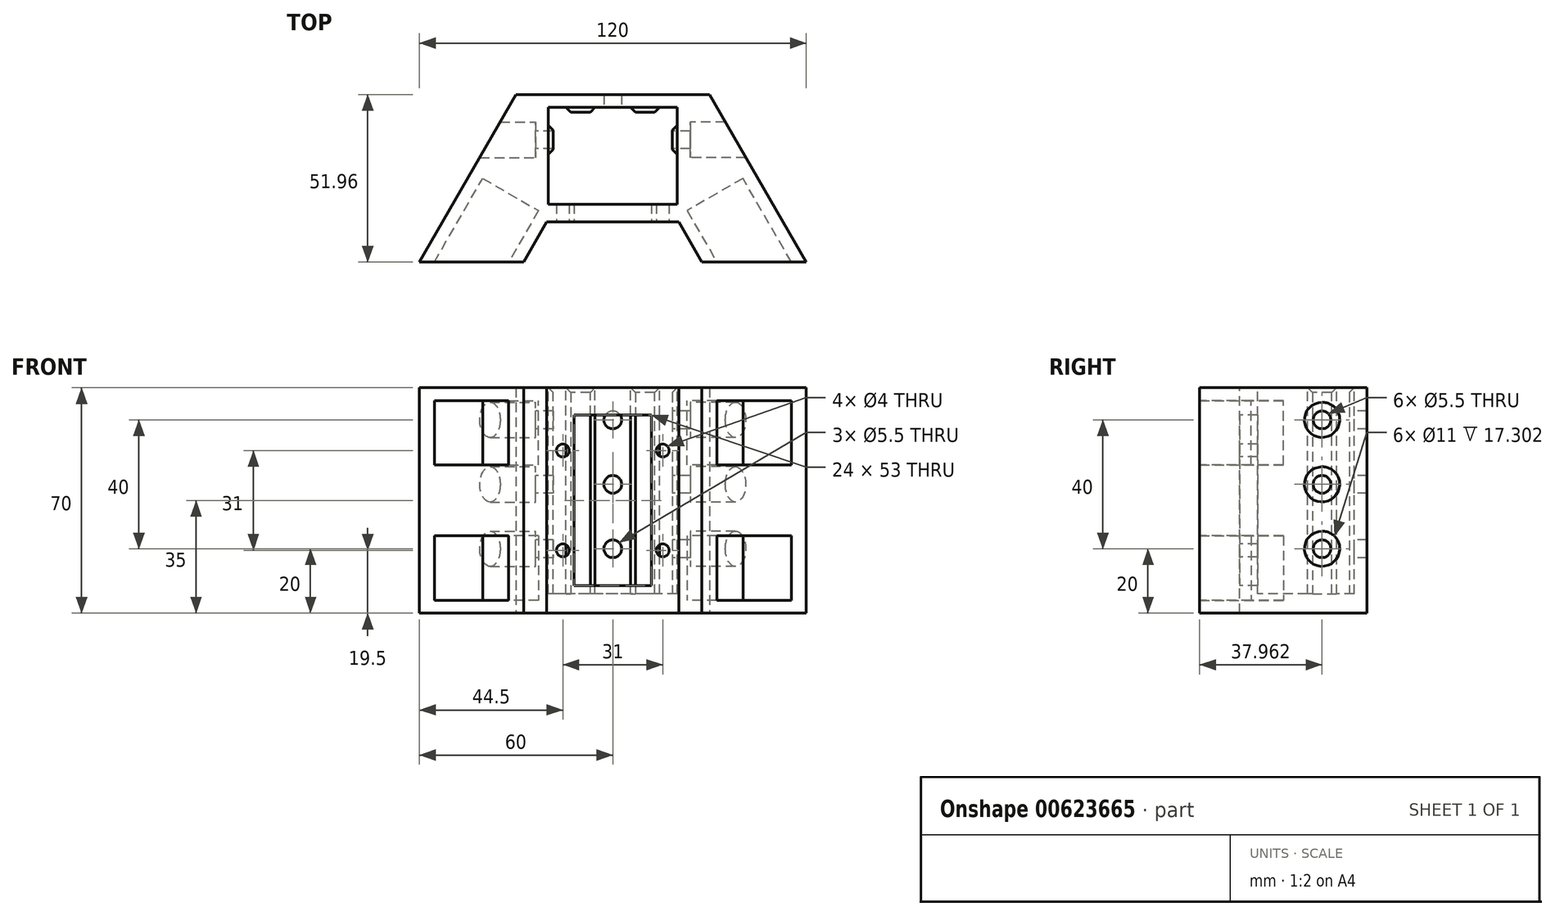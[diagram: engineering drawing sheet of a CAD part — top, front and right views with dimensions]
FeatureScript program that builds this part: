
annotation { "Feature Type Name" : "Feature", "Feature Type Description" : "" }
export const myFeature = defineFeature(function(context is Context, id is Id, definition is map)
    precondition{}
    {
        {
            var Q0;
            Q0=qCreatedBy(makeId("Top.planeOp"),FACE);
            var sketch = newSketch(context, id + "F0", { "sketchPlane" : qUnion([Q0])});
            skLineSegment(sketch, "E0", {"start": v(0, 0) * mm, "end": v(30, 51.96) * mm});
            skLineSegment(sketch, "E1", {"start": v(30, 51.96) * mm, "end": v(90, 51.96) * mm});
            skLineSegment(sketch, "E2", {"start": v(90, 51.96) * mm, "end": v(120, 0) * mm});
            skLineSegment(sketch, "E3", {"start": v(120, 0) * mm, "end": v(0, 0) * mm});
            skSolve(sketch);
        }
        {
            var Q0;
            Q0 = qSketchRegion(id + "F0", true);
            extrude(context, id + "F1", {"entities" : qUnion([Q0]), "depth" : 70 * mm, "offsetDistance" : 25 * mm});
        }
        {
            var Q0;
            Q0=makeQuery(id+"F1.opExtrude","CAP_FACE",FACE,{"disambiguationData":[OSD([sQuery(id+"F0.wireOp",EDGE,"E0"),sQuery(id+"F0.wireOp",EDGE,"E1"),sQuery(id+"F0.wireOp",EDGE,"E2"),sQuery(id+"F0.wireOp",EDGE,"E3")])],"isStart":false});
            var sketch = newSketch(context, id + "F2", { "sketchPlane" : qUnion([Q0])});
            skLineSegment(sketch, "E4.bottom", {"start": v(80, 47.96) * mm, "end": v(40, 47.96) * mm});
            skLineSegment(sketch, "E4.top", {"start": v(80, 27.96) * mm, "end": v(40, 27.96) * mm});
            skLineSegment(sketch, "E4.left", {"start": v(80, 47.96) * mm, "end": v(80, 27.96) * mm});
            skLineSegment(sketch, "E4.right", {"start": v(40, 47.96) * mm, "end": v(40, 27.96) * mm});
            skPoint(sketch, "E4.middle", {"position": v(60, 37.96) * mm});
            skPoint(sketch, "E4.middle.positionSnap0", {"position": v(60, 51.96) * mm});
            skPoint(sketch, "E4.centerSnap0", {"position": v(60, 51.96) * mm});
            skSolve(sketch);
        }
        {
            var Q0;
            Q0=makeQuery(id+"F2.imprint","IMPRINT",FACE,{"disambiguationData":[TD([[makeQuery(id+"F2.imprint","IMPRINT",EDGE,{"derivedFrom":sQuery(id+"F2.wireOp",EDGE,"E4.bottom")}),1.0]])]});
            extrude(context, id + "F3", {"entities" : qUnion([Q0]), "operationType" : NewBodyOperationType.REMOVE, "oppositeDirection" : true, "depth" : 64 * mm, "offsetDistance" : 25 * mm});
        }
        {
            var Q0;
            Q0=makeQuery(id+"F1.opExtrude","CAP_FACE",FACE,{"disambiguationData":[OSD([sQuery(id+"F0.wireOp",EDGE,"E0"),sQuery(id+"F0.wireOp",EDGE,"E1"),sQuery(id+"F0.wireOp",EDGE,"E2"),sQuery(id+"F0.wireOp",EDGE,"E3")])],"isStart":false});
            cPlane(context, id + "F4", {"entities" : qUnion([Q0]), "cplaneType" : CPlaneType.OFFSET, "offset" : 66 * mm, "oppositeDirection" : true, "width" : 150 * mm, "height" : 150 * mm});
        }
        {
            var Q0;
            Q0=qCreatedBy(id+"F4.planeOp",FACE);
            var sketch = newSketch(context, id + "F5", { "sketchPlane" : qUnion([Q0])});
            skLineSegment(sketch, "E5.0.0", {"start": v(0, 0) * mm, "end": v(120, 0) * mm, "construction": true});
            skLineSegment(sketch, "E5.0.1", {"start": v(120, 0) * mm, "end": v(90, 51.96) * mm, "construction": true});
            skLineSegment(sketch, "E5.0.2", {"start": v(90, 51.96) * mm, "end": v(30, 51.96) * mm, "construction": true});
            skLineSegment(sketch, "E5.0.3", {"start": v(30, 51.96) * mm, "end": v(0, 0) * mm, "construction": true});
            skLineSegment(sketch, "E6", {"start": v(4.62, 0) * mm, "end": v(19.62, 25.98) * mm});
            skLineSegment(sketch, "E7", {"start": v(19.62, 25.98) * mm, "end": v(36.94, 15.98) * mm});
            skLineSegment(sketch, "E8", {"start": v(36.94, 15.98) * mm, "end": v(27.71, 0) * mm});
            skLineSegment(sketch, "E9", {"start": v(27.71, 0) * mm, "end": v(4.62, 0) * mm});
            skLineSegment(sketch, "E10", {"start": v(60, 51.96) * mm, "end": v(60, 0) * mm, "construction": true});
            skLineSegment(sketch, "E11.MirrorCS", {"start": v(83.06, 15.98) * mm, "end": v(92.29, 0) * mm});
            skLineSegment(sketch, "E12.MirrorCS", {"start": v(100.38, 25.98) * mm, "end": v(83.06, 15.98) * mm});
            skLineSegment(sketch, "E13.MirrorCS", {"start": v(115.38, 0) * mm, "end": v(100.38, 25.98) * mm});
            skLineSegment(sketch, "E14", {"start": v(92.29, 0) * mm, "end": v(115.38, 0) * mm});
            skSolve(sketch);
        }
        {
            var Q0;
            Q0 = qSketchRegion(id + "F5", true);
            extrude(context, id + "F6", {"entities" : qUnion([Q0]), "operationType" : NewBodyOperationType.REMOVE, "depth" : 20 * mm, "offsetDistance" : 25 * mm});
        }
        {
            var Q0;
            Q0=makeQuery(id+"F1.opExtrude","CAP_FACE",FACE,{"disambiguationData":[OSD([sQuery(id+"F0.wireOp",EDGE,"E0"),sQuery(id+"F0.wireOp",EDGE,"E1"),sQuery(id+"F0.wireOp",EDGE,"E2"),sQuery(id+"F0.wireOp",EDGE,"E3")])],"isStart":false});
            cPlane(context, id + "F7", {"entities" : qUnion([Q0]), "cplaneType" : CPlaneType.OFFSET, "offset" : 4 * mm, "oppositeDirection" : true, "width" : 150 * mm, "height" : 150 * mm});
        }
        {
            var Q0;
            Q0=qCreatedBy(id+"F7.planeOp",FACE);
            var sketch = newSketch(context, id + "F8", { "sketchPlane" : qUnion([Q0])});
            skLineSegment(sketch, "E15.0.0", {"start": v(4.62, 0) * mm, "end": v(27.71, 0) * mm});
            skLineSegment(sketch, "E15.0.1", {"start": v(27.71, 0) * mm, "end": v(36.94, 15.98) * mm});
            skLineSegment(sketch, "E15.0.2", {"start": v(36.94, 15.98) * mm, "end": v(19.62, 25.98) * mm});
            skLineSegment(sketch, "E15.0.3", {"start": v(19.62, 25.98) * mm, "end": v(4.62, 0) * mm});
            skLineSegment(sketch, "E16.0.0", {"start": v(83.06, 15.98) * mm, "end": v(92.29, 0) * mm});
            skLineSegment(sketch, "E16.0.1", {"start": v(92.29, 0) * mm, "end": v(115.38, 0) * mm});
            skLineSegment(sketch, "E16.0.2", {"start": v(115.38, 0) * mm, "end": v(100.38, 25.98) * mm});
            skLineSegment(sketch, "E16.0.3", {"start": v(100.38, 25.98) * mm, "end": v(83.06, 15.98) * mm});
            skSolve(sketch);
        }
        {
            var Q0;
            Q0 = qSketchRegion(id + "F8", true);
            extrude(context, id + "F9", {"entities" : qUnion([Q0]), "operationType" : NewBodyOperationType.REMOVE, "oppositeDirection" : true, "depth" : 20 * mm, "offsetDistance" : 25 * mm});
        }
        {
            var Q0;
            Q0=makeQuery(id+"F1.opExtrude","CAP_FACE",FACE,{"disambiguationData":[OSD([sQuery(id+"F0.wireOp",EDGE,"E0"),sQuery(id+"F0.wireOp",EDGE,"E1"),sQuery(id+"F0.wireOp",EDGE,"E2"),sQuery(id+"F0.wireOp",EDGE,"E3")])],"isStart":false});
            var sketch = newSketch(context, id + "F10", { "sketchPlane" : qUnion([Q0])});
            skLineSegment(sketch, "E17.0.0", {"start": v(36.94, 15.98) * mm, "end": v(19.62, 25.98) * mm, "construction": true});
            skLineSegment(sketch, "E17.0.1", {"start": v(19.62, 25.98) * mm, "end": v(4.62, 0) * mm, "construction": true});
            skLineSegment(sketch, "E17.0.2", {"start": v(4.62, 0) * mm, "end": v(27.71, 0) * mm, "construction": true});
            skLineSegment(sketch, "E17.0.3", {"start": v(27.71, 0) * mm, "end": v(36.94, 15.98) * mm, "construction": true});
            skLineSegment(sketch, "E18.0.0", {"start": v(115.38, 0) * mm, "end": v(100.38, 25.98) * mm, "construction": true});
            skLineSegment(sketch, "E18.0.1", {"start": v(100.38, 25.98) * mm, "end": v(83.06, 15.98) * mm, "construction": true});
            skLineSegment(sketch, "E18.0.2", {"start": v(83.06, 15.98) * mm, "end": v(92.29, 0) * mm, "construction": true});
            skLineSegment(sketch, "E18.0.3", {"start": v(92.29, 0) * mm, "end": v(115.38, 0) * mm, "construction": true});
            skLineSegment(sketch, "E19", {"start": v(32.33, 0) * mm, "end": v(39.5, 12.42) * mm});
            skLineSegment(sketch, "E20", {"start": v(39.5, 12.42) * mm, "end": v(80.5, 12.42) * mm});
            skLineSegment(sketch, "E21", {"start": v(80.5, 12.42) * mm, "end": v(87.67, 0) * mm});
            skLineSegment(sketch, "E22", {"start": v(87.67, 0) * mm, "end": v(32.33, 0) * mm});
            skSolve(sketch);
        }
        {
            var Q0;
            Q0=makeQuery(id+"F10.imprint","IMPRINT",FACE,{"disambiguationData":[TD([[makeQuery(id+"F10.imprint","IMPRINT",EDGE,{"derivedFrom":sQuery(id+"F10.wireOp",EDGE,"E19")}),-1.0]])]});
            extrude(context, id + "F11", {"entities" : qUnion([Q0]), "operationType" : NewBodyOperationType.REMOVE, "endBound" : BoundingType.THROUGH_ALL, "oppositeDirection" : true, "depth" : 25 * mm, "offsetDistance" : 25 * mm});
        }
        {
            var Q0;
            Q0=makeQuery(id+"F11.boolean.opBoolean","COPY",FACE,{"derivedFrom":makeQuery(id+"F11.opExtrude","SWEPT_FACE",FACE,{"disambiguationData":[OSD([sQuery(id+"F10.wireOp",EDGE,"E20")])]})});
            var sketch = newSketch(context, id + "F12", { "sketchPlane" : qUnion([Q0])});
            skLineSegment(sketch, "E23.0", {"start": v(48, 8.5) * mm, "end": v(72, 8.5) * mm});
            skLineSegment(sketch, "E23.1", {"start": v(48, 61.5) * mm, "end": v(48, 8.5) * mm});
            skLineSegment(sketch, "E23.2", {"start": v(72, 61.5) * mm, "end": v(48, 61.5) * mm});
            skLineSegment(sketch, "E23.3", {"start": v(72, 8.5) * mm, "end": v(72, 61.5) * mm});
            skSolve(sketch);
        }
        {
            var Q0;
            Q0=makeQuery(id+"F12.imprint","IMPRINT",FACE,{"disambiguationData":[TD([[makeQuery(id+"F12.imprint","IMPRINT",EDGE,{"derivedFrom":sQuery(id+"F12.wireOp",EDGE,"E23.0")}),1.0]])]});
            extrude(context, id + "F13", {"entities" : qUnion([Q0]), "operationType" : NewBodyOperationType.REMOVE, "endBound" : BoundingType.UP_TO_NEXT, "oppositeDirection" : true, "depth" : 25 * mm, "offsetDistance" : 25 * mm});
        }
        {
            var Q0;
            Q0=makeQuery(id+"F11.boolean.opBoolean","COPY",FACE,{"derivedFrom":makeQuery(id+"F11.opExtrude","SWEPT_FACE",FACE,{"disambiguationData":[OSD([sQuery(id+"F10.wireOp",EDGE,"E20")])]})});
            var sketch = newSketch(context, id + "F14", { "sketchPlane" : qUnion([Q0])});
            skCircle(sketch, "E24", {"center": v(44.5, 50.5) * mm, "radius": 2 * mm});
            skCircle(sketch, "E25", {"center": v(44.5, 19.5) * mm, "radius": 2 * mm});
            skCircle(sketch, "E26", {"center": v(75.5, 19.5) * mm, "radius": 2 * mm});
            skCircle(sketch, "E27", {"center": v(75.5, 50.5) * mm, "radius": 2 * mm});
            skSolve(sketch);
        }
        {
            var Q0;
            Q0 = qSketchRegion(id + "F14", true);
            extrude(context, id + "F15", {"entities" : qUnion([Q0]), "operationType" : NewBodyOperationType.REMOVE, "endBound" : BoundingType.UP_TO_NEXT, "oppositeDirection" : true, "depth" : 25 * mm, "offsetDistance" : 25 * mm});
        }
        {
            var Q0;
            Q0=makeQuery(id+"F3.boolean.opBoolean","COPY",FACE,{"derivedFrom":makeQuery(id+"F3.opExtrude","SWEPT_FACE",FACE,{"disambiguationData":[OSD([sQuery(id+"F2.wireOp",EDGE,"E4.top")])]})});
            extrude(context, id + "F16", {"entities" : qUnion([Q0]), "operationType" : NewBodyOperationType.REMOVE, "oppositeDirection" : true, "depth" : 10 * mm, "offsetDistance" : 25 * mm});
        }
        {
            var Q0;
            Q0=makeQuery(id+"F1.opExtrude","CAP_FACE",FACE,{"disambiguationData":[OSD([sQuery(id+"F0.wireOp",EDGE,"E0"),sQuery(id+"F0.wireOp",EDGE,"E1"),sQuery(id+"F0.wireOp",EDGE,"E2"),sQuery(id+"F0.wireOp",EDGE,"E3")])],"isStart":false});
            var sketch = newSketch(context, id + "F17", { "sketchPlane" : qUnion([Q0])});
            skLineSegment(sketch, "E28.bottom", {"start": v(40, 42.46) * mm, "end": v(41.5, 42.46) * mm});
            skLineSegment(sketch, "E28.top", {"start": v(40, 33.46) * mm, "end": v(41.5, 33.46) * mm});
            skLineSegment(sketch, "E28.left", {"start": v(40, 42.46) * mm, "end": v(40, 33.46) * mm});
            skLineSegment(sketch, "E28.right", {"start": v(41.5, 42.46) * mm, "end": v(41.5, 33.46) * mm});
            skLineSegment(sketch, "E29.bottom", {"start": v(45.5, 47.96) * mm, "end": v(54.5, 47.96) * mm});
            skLineSegment(sketch, "E29.top", {"start": v(45.5, 46.46) * mm, "end": v(54.5, 46.46) * mm});
            skLineSegment(sketch, "E29.left", {"start": v(45.5, 47.96) * mm, "end": v(45.5, 46.46) * mm});
            skLineSegment(sketch, "E29.right", {"start": v(54.5, 47.96) * mm, "end": v(54.5, 46.46) * mm});
            skLineSegment(sketch, "E30.bottom", {"start": v(80, 42.46) * mm, "end": v(78.5, 42.46) * mm});
            skLineSegment(sketch, "E30.top", {"start": v(80, 33.46) * mm, "end": v(78.5, 33.46) * mm});
            skLineSegment(sketch, "E30.left", {"start": v(80, 42.46) * mm, "end": v(80, 33.46) * mm});
            skLineSegment(sketch, "E30.right", {"start": v(78.5, 42.46) * mm, "end": v(78.5, 33.46) * mm});
            skLineSegment(sketch, "E31.bottom", {"start": v(65.5, 47.96) * mm, "end": v(74.5, 47.96) * mm});
            skLineSegment(sketch, "E31.top", {"start": v(65.5, 46.46) * mm, "end": v(74.5, 46.46) * mm});
            skLineSegment(sketch, "E31.left", {"start": v(65.5, 47.96) * mm, "end": v(65.5, 46.46) * mm});
            skLineSegment(sketch, "E31.right", {"start": v(74.5, 47.96) * mm, "end": v(74.5, 46.46) * mm});
            skSolve(sketch);
        }
        {
            var Q0;
            Q0 = qSketchRegion(id + "F17", true);
            var Q1;
            {var subQ0=sQuery(id+"F2.wireOp",EDGE,"E4.top");Q1=makeQuery(id+"F16.boolean.opBoolean","MERGE",FACE,{"derivedFrom":[makeQuery(id+"F3.boolean.opBoolean","COPY",FACE,{"derivedFrom":makeQuery(id+"F3.opExtrude","CAP_FACE",FACE,{"disambiguationData":[OSD([sQuery(id+"F2.wireOp",EDGE,"E4.bottom"),subQ0,sQuery(id+"F2.wireOp",EDGE,"E4.left"),sQuery(id+"F2.wireOp",EDGE,"E4.right")])],"isStart":false})}),makeQuery(id+"F16.opExtrude","SWEPT_FACE",FACE,{"disambiguationData":[OSD([subQ0]),TDD([makeQuery(id+"F3.boolean.opBoolean","COPY",EDGE,{"derivedFrom":makeQuery(id+"F3.opExtrude","CAP_EDGE",EDGE,{"disambiguationData":[OSD([subQ0])],"isStart":false})})])]})]});}
            extrude(context, id + "F18", {"entities" : qUnion([Q0]), "operationType" : NewBodyOperationType.ADD, "endBound" : BoundingType.UP_TO_SURFACE, "oppositeDirection" : true, "depth" : 25 * mm, "endBoundEntityFace" : qUnion([Q1]), "offsetDistance" : 25 * mm});
        }
        {
            var Q0;
            Q0=makeQuery(id+"F18.opExtrude","SWEPT_EDGE",EDGE,{"disambiguationData":[OSD([sQuery(id+"F17.wireOp",EDGE,"E29.top"),sQuery(id+"F17.wireOp",EDGE,"E29.right")])]});
            var Q1;
            Q1=makeQuery(id+"F18.opExtrude","SWEPT_EDGE",EDGE,{"disambiguationData":[OSD([sQuery(id+"F17.wireOp",EDGE,"E29.top"),sQuery(id+"F17.wireOp",EDGE,"E29.left")])]});
            var Q2;
            Q2=makeQuery(id+"F18.opExtrude","CAP_EDGE",EDGE,{"disambiguationData":[OSD([sQuery(id+"F17.wireOp",EDGE,"E29.top")])],"isStart":true});
            var Q3;
            Q3=makeQuery(id+"F18.opExtrude","CAP_EDGE",EDGE,{"disambiguationData":[OSD([sQuery(id+"F17.wireOp",EDGE,"E28.right")])],"isStart":true});
            var Q4;
            Q4=makeQuery(id+"F18.opExtrude","SWEPT_EDGE",EDGE,{"disambiguationData":[OSD([sQuery(id+"F17.wireOp",EDGE,"E28.top"),sQuery(id+"F17.wireOp",EDGE,"E28.right")])]});
            var Q5;
            Q5=makeQuery(id+"F18.opExtrude","SWEPT_EDGE",EDGE,{"disambiguationData":[OSD([sQuery(id+"F17.wireOp",EDGE,"E31.top"),sQuery(id+"F17.wireOp",EDGE,"E31.left")])]});
            var Q6;
            Q6=makeQuery(id+"F18.opExtrude","SWEPT_EDGE",EDGE,{"disambiguationData":[OSD([sQuery(id+"F17.wireOp",EDGE,"E31.top"),sQuery(id+"F17.wireOp",EDGE,"E31.right")])]});
            var Q7;
            Q7=makeQuery(id+"F18.opExtrude","SWEPT_EDGE",EDGE,{"disambiguationData":[OSD([sQuery(id+"F17.wireOp",EDGE,"E30.top"),sQuery(id+"F17.wireOp",EDGE,"E30.right")])]});
            var Q8;
            Q8=makeQuery(id+"F18.opExtrude","SWEPT_EDGE",EDGE,{"disambiguationData":[OSD([sQuery(id+"F17.wireOp",EDGE,"E30.bottom"),sQuery(id+"F17.wireOp",EDGE,"E30.right")])]});
            var Q9;
            Q9=makeQuery(id+"F18.opExtrude","CAP_EDGE",EDGE,{"disambiguationData":[OSD([sQuery(id+"F17.wireOp",EDGE,"E31.top")])],"isStart":true});
            var Q10;
            Q10=makeQuery(id+"F18.opExtrude","CAP_EDGE",EDGE,{"disambiguationData":[OSD([sQuery(id+"F17.wireOp",EDGE,"E30.right")])],"isStart":true});
            var Q11;
            Q11=makeQuery(id+"F18.opExtrude","SWEPT_EDGE",EDGE,{"disambiguationData":[OSD([sQuery(id+"F17.wireOp",EDGE,"E28.bottom"),sQuery(id+"F17.wireOp",EDGE,"E28.right")])]});
            chamfer(context, id + "F19", {"entities" : qUnion([Q0, Q1, Q2, Q3, Q4, Q5, Q6, Q7, Q8, Q9, Q10, Q11]), "width" : 1.5 * mm, "tangentPropagation" : true});
        }
        {
            var Q0;
            Q0=makeQuery(id+"F18.opExtrude","SWEPT_FACE",FACE,{"disambiguationData":[OSD([sQuery(id+"F17.wireOp",EDGE,"E30.right")])]});
            var sketch = newSketch(context, id + "F20", { "sketchPlane" : qUnion([Q0])});
            skCircle(sketch, "E32", {"center": v(-37.96, 60) * mm, "radius": 2.75 * mm});
            skPoint(sketch, "E32.centerSnap0", {"position": v(-37.96, 68.5) * mm});
            skCircle(sketch, "E33.0.1.0", {"center": v(-37.96, 40) * mm, "radius": 2.75 * mm});
            skCircle(sketch, "E33.0.2.0", {"center": v(-37.96, 20) * mm, "radius": 2.75 * mm});
            skLineSegment(sketch, "E33.direction1", {"start": v(-37.96, 60) * mm, "end": v(-12.96, 60) * mm, "construction": true});
            skLineSegment(sketch, "E33.direction2", {"start": v(-37.96, 60) * mm, "end": v(-37.96, 40) * mm, "construction": true});
            skSolve(sketch);
        }
        {
            var Q0;
            Q0 = qSketchRegion(id + "F20", true);
            extrude(context, id + "F21", {"entities" : qUnion([Q0]), "operationType" : NewBodyOperationType.REMOVE, "endBound" : BoundingType.THROUGH_ALL, "oppositeDirection" : true, "depth" : 25 * mm, "offsetDistance" : 25 * mm, "hasSecondDirection" : true, "secondDirectionBound" : SecondDirectionBoundingType.THROUGH_ALL, "secondDirectionOppositeDirection" : false, "secondDirectionDepth" : 25 * mm});
        }
        {
            var Q0;
            {var subQ0=sQuery(id+"F2.wireOp",EDGE,"E4.top");var subQ2=sQuery(id+"F2.wireOp",EDGE,"E4.left");Q0=makeQuery(id+"F18.boolean.opBoolean","SPLIT",FACE,{"disambiguationData":[TD([makeQuery(id+"F16.boolean.opBoolean","COPY",FACE,{"derivedFrom":makeQuery(id+"F16.opExtrude","CAP_FACE",FACE,{"disambiguationData":[OSD([subQ0])],"isStart":false})})])],"derivedFrom":makeQuery(id+"F16.boolean.opBoolean","MERGE",FACE,{"derivedFrom":[makeQuery(id+"F3.boolean.opBoolean","COPY",FACE,{"derivedFrom":makeQuery(id+"F3.opExtrude","SWEPT_FACE",FACE,{"disambiguationData":[OSD([subQ2])]})})],"fromTools":[makeQuery(id+"F16.opExtrude","SWEPT_FACE",FACE,{"disambiguationData":[OSD([subQ0,subQ2])]})]})});}
            cPlane(context, id + "F22", {"entities" : qUnion([Q0]), "cplaneType" : CPlaneType.OFFSET, "offset" : 4 * mm, "oppositeDirection" : true, "width" : 150 * mm, "height" : 150 * mm});
        }
        {
            var Q0;
            {var subQ0=sQuery(id+"F2.wireOp",EDGE,"E4.top");var subQ1=sQuery(id+"F2.wireOp",EDGE,"E4.right");Q0=makeQuery(id+"F18.boolean.opBoolean","SPLIT",FACE,{"disambiguationData":[TD([makeQuery(id+"F16.boolean.opBoolean","COPY",FACE,{"derivedFrom":makeQuery(id+"F16.opExtrude","CAP_FACE",FACE,{"disambiguationData":[OSD([subQ0])],"isStart":false})})])],"derivedFrom":makeQuery(id+"F16.boolean.opBoolean","MERGE",FACE,{"derivedFrom":[makeQuery(id+"F3.boolean.opBoolean","COPY",FACE,{"derivedFrom":makeQuery(id+"F3.opExtrude","SWEPT_FACE",FACE,{"disambiguationData":[OSD([subQ1])]})})],"fromTools":[makeQuery(id+"F16.opExtrude","SWEPT_FACE",FACE,{"disambiguationData":[OSD([subQ0,subQ1])]})]})});}
            cPlane(context, id + "F23", {"entities" : qUnion([Q0]), "cplaneType" : CPlaneType.OFFSET, "offset" : 4 * mm, "oppositeDirection" : true, "width" : 150 * mm, "height" : 150 * mm});
        }
        {
            var Q0;
            Q0=qCreatedBy(id+"F22.planeOp",FACE);
            var sketch = newSketch(context, id + "F24", { "sketchPlane" : qUnion([Q0])});
            skCircle(sketch, "E34.0", {"center": v(-37.96, 60) * mm, "radius": 2.75 * mm, "construction": true});
            skCircle(sketch, "E35.0", {"center": v(-37.96, 40) * mm, "radius": 2.75 * mm, "construction": true});
            skCircle(sketch, "E36.0", {"center": v(-37.96, 20) * mm, "radius": 2.75 * mm, "construction": true});
            skCircle(sketch, "E37", {"center": v(-37.96, 60) * mm, "radius": 5.5 * mm});
            skCircle(sketch, "E38", {"center": v(-37.96, 40) * mm, "radius": 5.5 * mm});
            skCircle(sketch, "E39", {"center": v(-37.96, 20) * mm, "radius": 5.5 * mm});
            skSolve(sketch);
        }
        {
            var Q0;
            Q0 = qSketchRegion(id + "F24", true);
            extrude(context, id + "F25", {"entities" : qUnion([Q0]), "operationType" : NewBodyOperationType.REMOVE, "endBound" : BoundingType.THROUGH_ALL, "oppositeDirection" : true, "depth" : 25 * mm, "offsetDistance" : 25 * mm});
        }
        {
            var Q0;
            Q0=qCreatedBy(id+"F23.planeOp",FACE);
            var sketch = newSketch(context, id + "F26", { "sketchPlane" : qUnion([Q0])});
            skCircle(sketch, "E40.0", {"center": v(37.96, 60) * mm, "radius": 5.5 * mm});
            skCircle(sketch, "E41.0", {"center": v(37.96, 40) * mm, "radius": 5.5 * mm});
            skCircle(sketch, "E42.0", {"center": v(37.96, 20) * mm, "radius": 5.5 * mm});
            skSolve(sketch);
        }
        {
            var Q0;
            Q0 = qSketchRegion(id + "F26", true);
            extrude(context, id + "F27", {"entities" : qUnion([Q0]), "operationType" : NewBodyOperationType.REMOVE, "endBound" : BoundingType.THROUGH_ALL, "oppositeDirection" : true, "depth" : 25 * mm, "offsetDistance" : 25 * mm});
        }
        {
            var Q0;
            {var subQ0=sQuery(id+"F17.wireOp",EDGE,"E29.right");var subQ1=sQuery(id+"F2.wireOp",EDGE,"E4.bottom");Q0=makeQuery(id+"F18.boolean.opBoolean","SPLIT",FACE,{"disambiguationData":[TD([makeQuery(id+"F18.opExtrude","SWEPT_FACE",FACE,{"disambiguationData":[OSD([subQ0])]})])],"derivedFrom":makeQuery(id+"F3.boolean.opBoolean","COPY",FACE,{"derivedFrom":makeQuery(id+"F3.opExtrude","SWEPT_FACE",FACE,{"disambiguationData":[OSD([subQ1])]})})});}
            var sketch = newSketch(context, id + "F28", { "sketchPlane" : qUnion([Q0])});
            skCircle(sketch, "E43", {"center": v(60, 60) * mm, "radius": 2.75 * mm});
            skPoint(sketch, "E43.centerSnap0", {"position": v(60, 70) * mm});
            skCircle(sketch, "E44", {"center": v(60, 40) * mm, "radius": 2.75 * mm});
            skCircle(sketch, "E45", {"center": v(60, 20) * mm, "radius": 2.75 * mm});
            skSolve(sketch);
        }
        {
            var Q0;
            Q0 = qSketchRegion(id + "F28", true);
            extrude(context, id + "F29", {"entities" : qUnion([Q0]), "operationType" : NewBodyOperationType.REMOVE, "endBound" : BoundingType.THROUGH_ALL, "oppositeDirection" : true, "depth" : 25 * mm, "offsetDistance" : 25 * mm});
        }
    });
